# Revit family: Doors_Industrial_Wayne-Dalton_Rolling-Service-Doors-Model-926_
name_source: partatom
category: Specialty Equipment
units: mm (PartAtom-declared; Revit-internal decimal feet)

## family parameters
Always vertical = Yes
Cut with Voids When Loaded = Yes
Host = Wall
OmniClass Number = 23.30.10.21.34
OmniClass Title = Industrial Doors
Part Type = Normal
Room Calculation Point = No
Round Connector Dimension = Use Diameter
Shared = No

## types (6) — shared parameters
Connector Array Distance = 0"
Current = 20 A
Description = Model 926 Rolling Service Door
Finish Material = Finish - Wayne Dalton - Black
Frequency = 60 Hz
Manufacturer = Wayne Dalton
Model = 926
Powder Coat (Note) = Wayne Dalton also offers approximately 200 RAL powder coat options to complement the exterior colors of a building.
Power Factor = 1
Product Guid = fe4d908b-e8df-4d50-a579-f2ac10b2d6b5
Product Page URL = https://www.wayne-dalton.com
Product data url = https://www.bimobject.com
URL = https://www.wayne-dalton.com
Wall Closure = By host

## per-type parameters (varying)
| type | Apparent Load Phase 1 | Apparent Load Phase 2 | Apparent Load Phase 3 | Connector Array | Number of Poles | Operator Visibility | Voltage |
| 115 volts, one phase, 60 Hz (110-120V range) | 2300 VA | 0 VA | 0 VA | 3 | 1 | Yes | 115 V |
| Chain Hoist | 2300 VA | 0 VA | 0 VA | 2 | 1 | Yes | 115 V |
| Manual push-up | 2300 VA | 0 VA | 0 VA | 2 | 1 | No | 115 V |
| 230 volts, three phase, 60 Hz (208-245V range) | 2656 VA | 2656 VA | 2656 VA | 3 | 3 | Yes | 230 V |
| 230 volts, single phase, 60 Hz (208-245V range) | 4600 VA | 0 VA | 0 VA | 3 | 1 | Yes | 230 V |
| 460 volts, three phase, 60 Hz (456-495V range) | 5312 VA | 5312 VA | 5312 VA | 3 | 3 | Yes | 460 V |

type visibility flags (boolean, named after types; folded from table):
- 115 volts, one phase, 60 Hz (110-120V range): Yes: (none)
- Chain Hoist: Yes: Chain Hoist or Manual
- Manual push-up: Yes: Chain Hoist or Manual
- 230 volts, three phase, 60 Hz (208-245V range): Yes: (none)
- 230 volts, single phase, 60 Hz (208-245V range): Yes: (none)
- 460 volts, three phase, 60 Hz (456-495V range): Yes: (none)

## geometry (parser evidence)
native form markers: Sweep x14
no freeform markers — native parametric forms only
